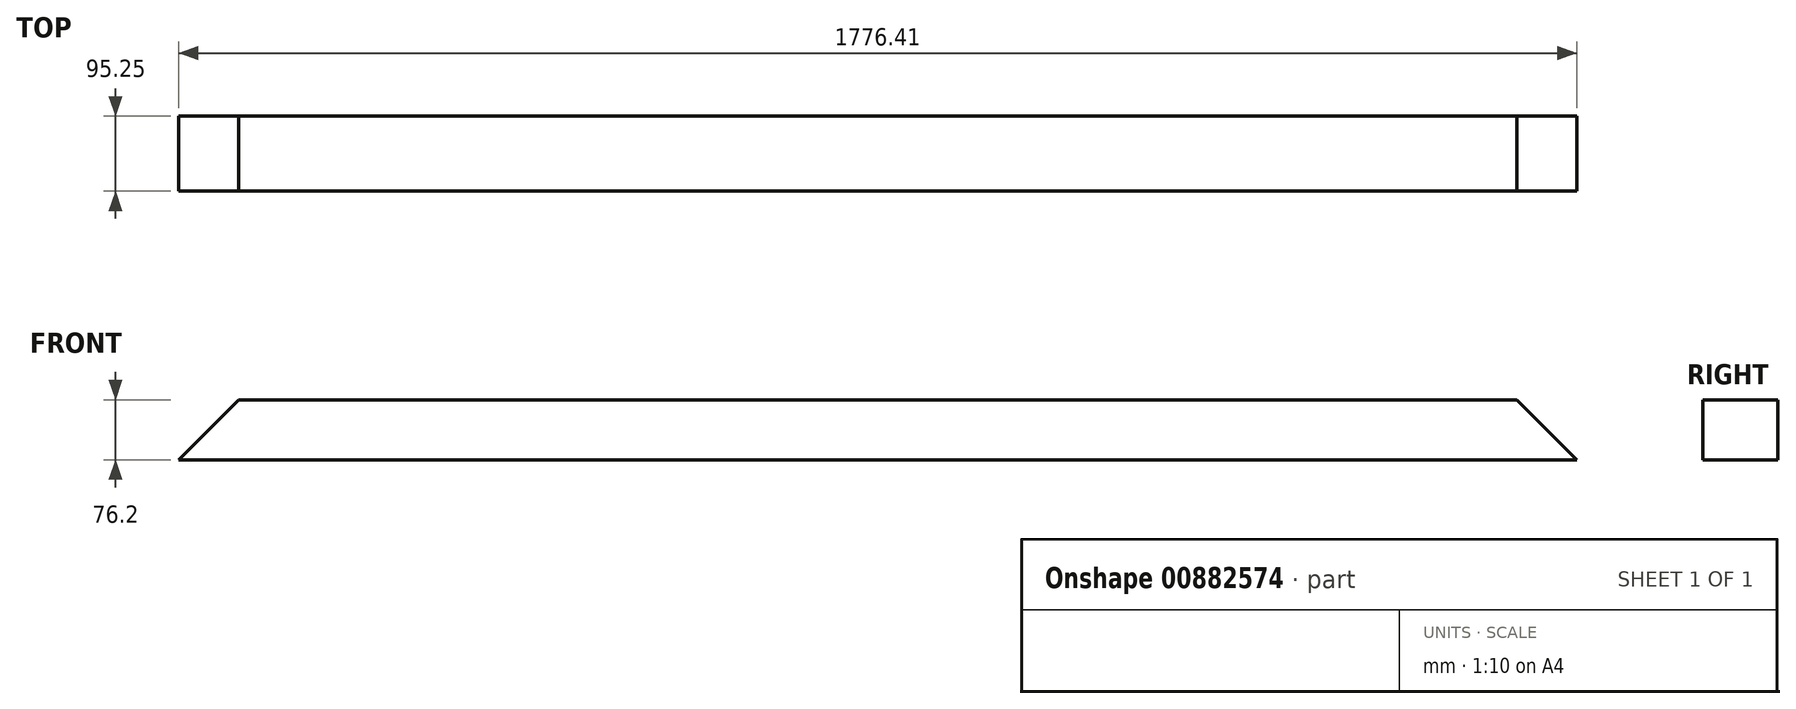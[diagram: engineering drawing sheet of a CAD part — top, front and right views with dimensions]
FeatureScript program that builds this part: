
annotation { "Feature Type Name" : "Feature", "Feature Type Description" : "" }
export const myFeature = defineFeature(function(context is Context, id is Id, definition is map)
    precondition{}
    {
        {
            var Q0;
            Q0=qCreatedBy(makeId("Right.planeOp"),FACE);
            var sketch = newSketch(context, id + "F0", { "sketchPlane" : qUnion([Q0])});
            skLineSegment(sketch, "E0.bottom", {"start": v(0, 0) * mm, "end": v(-95.25, 0) * mm});
            skLineSegment(sketch, "E0.top", {"start": v(0, -76.2) * mm, "end": v(-95.25, -76.2) * mm});
            skLineSegment(sketch, "E0.left", {"start": v(0, 0) * mm, "end": v(0, -76.2) * mm});
            skLineSegment(sketch, "E0.right", {"start": v(-95.25, 0) * mm, "end": v(-95.25, -76.2) * mm});
            skSolve(sketch);
        }
        {
            var Q0;
            Q0=makeQuery(id+"F0.imprint","IMPRINT",FACE,{"disambiguationData":[TD([[makeQuery(id+"F0.imprint","IMPRINT",EDGE,{"derivedFrom":sQuery(id+"F0.wireOp",EDGE,"E0.bottom")}),1.0]])]});
            extrude(context, id + "F1", {"entities" : qUnion([Q0]), "depth" : 1776.4 * mm, "offsetDistance" : 25.4 * mm});
        }
        {
            var Q0;
            Q0=makeQuery(id+"F1.opExtrude","SWEPT_FACE",FACE,{"disambiguationData":[OSD([sQuery(id+"F0.wireOp",EDGE,"E0.right")])]});
            var sketch = newSketch(context, id + "F2", { "sketchPlane" : qUnion([Q0])});
            skLineSegment(sketch, "E1", {"start": v(0, -76.2) * mm, "end": v(0, 0) * mm});
            skLineSegment(sketch, "E2", {"start": v(0, 0) * mm, "end": v(76.2, 0) * mm});
            skLineSegment(sketch, "E3", {"start": v(76.2, 0) * mm, "end": v(0, -76.2) * mm});
            skLineSegment(sketch, "E4", {"start": v(1776.41, 0) * mm, "end": v(1776.41, -76.2) * mm});
            skLineSegment(sketch, "E5", {"start": v(1776.41, -76.2) * mm, "end": v(1700.21, 0) * mm});
            skLineSegment(sketch, "E6", {"start": v(1700.21, 0) * mm, "end": v(1776.41, 0) * mm});
            skSolve(sketch);
        }
        {
            var Q0;
            Q0 = qSketchRegion(id + "F2", true);
            extrude(context, id + "F3", {"entities" : qUnion([Q0]), "operationType" : NewBodyOperationType.REMOVE, "endBound" : BoundingType.THROUGH_ALL, "oppositeDirection" : true, "depth" : 25.4 * mm, "offsetDistance" : 25.4 * mm});
        }
    });
